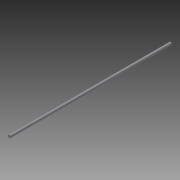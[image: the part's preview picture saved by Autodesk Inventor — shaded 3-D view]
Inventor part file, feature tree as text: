
AUTODESK INVENTOR PART (.ipt)
format: ipt  version: 2014 SP1 (Build 180222100, 222)  size: 63,488 bytes
history: native  units: in
note: dims shown in document units (in); Inventor stores cm internally (conversion verified against a paired STEP export)
features: extrude x1, sketch x1
ambient origin geometry x8: Origin, YZ Plane, XZ Plane, XY Plane, X Axis, Y Axis, Z Axis, Center Point
bodies: Solid1 (feature_tree)
feature tree (2):
  extrude  "Extrusion1"  Depth=14.0in TaperAngle=0.0deg
  sketch  "Sketch1"  dims[d0=0.2362in d1=14.0in d2=0.0in]
